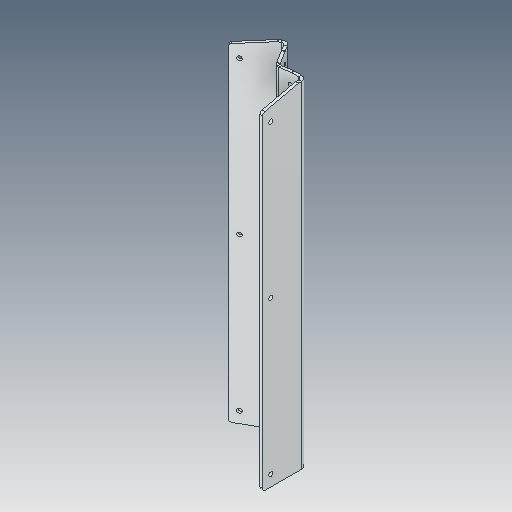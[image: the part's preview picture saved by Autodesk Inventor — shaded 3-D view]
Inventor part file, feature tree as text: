
AUTODESK INVENTOR PART (.ipt)
format: ipt  version: 2023.5 (Build 275446000, 446)  size: 138,752 bytes
history: native  units: in
note: dims shown in document units (in); Inventor stores cm internally (conversion verified against a paired STEP export)
features: fillet x1
ambient origin geometry x8: Origin, YZ Plane, XZ Plane, XY Plane, X Axis, Y Axis, Z Axis, Center Point
bodies: Solid1 (feature_tree)
feature tree (1):
  fillet  "Fillet2"  [1 undecoded]
note: 1 required parameter value undecoded (feature->parameter linkage not recoverable at this tier; creation-order binding heuristic only, values carry confidence <= 0.55)
